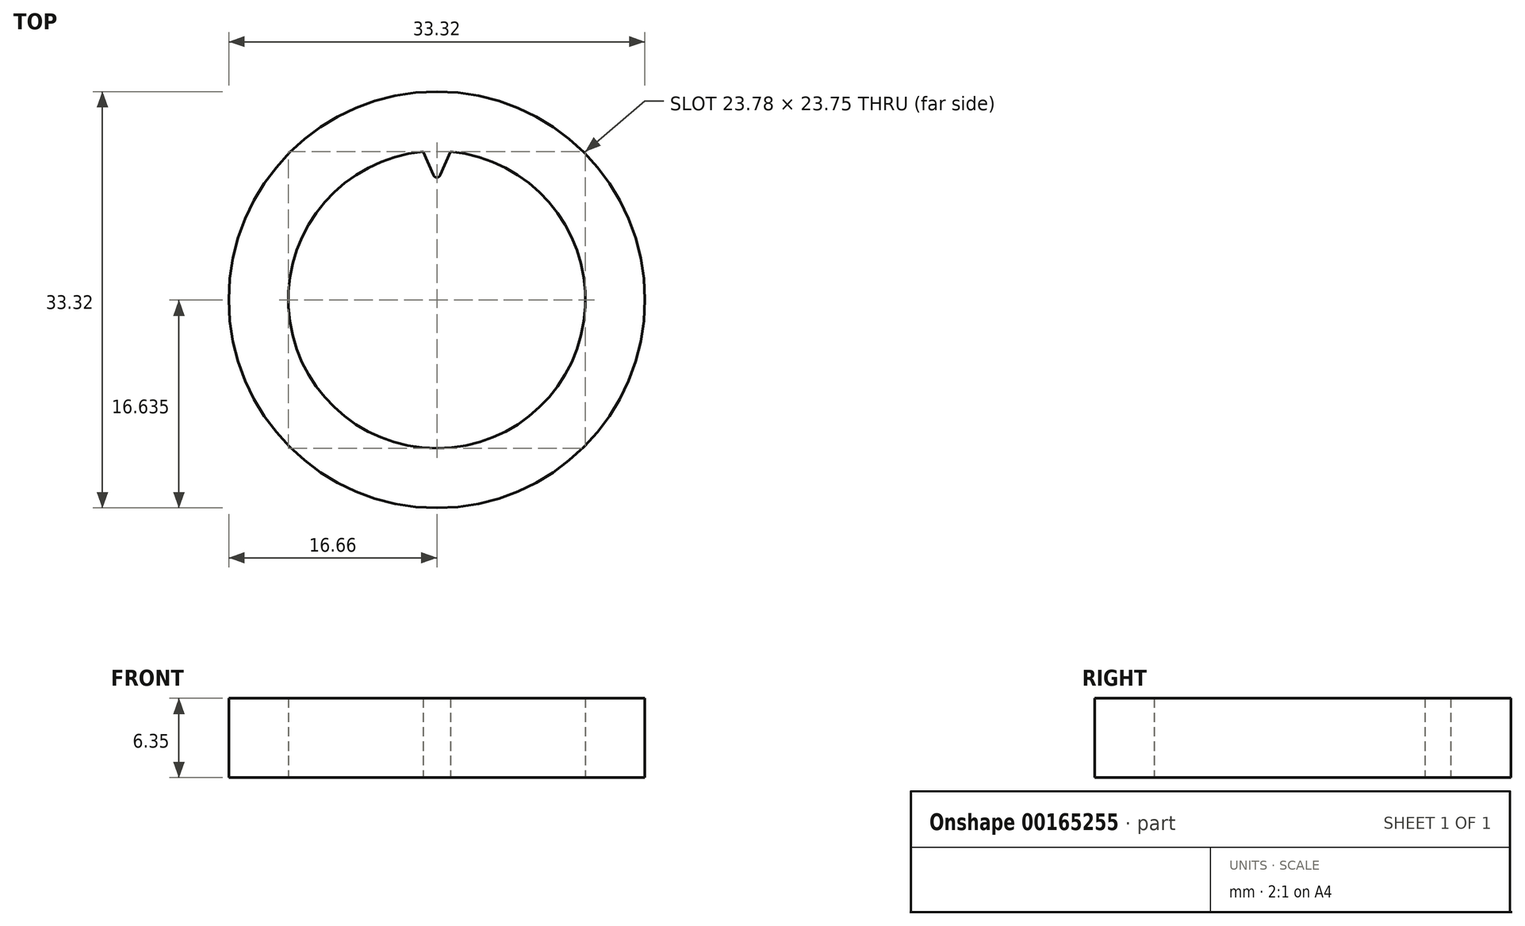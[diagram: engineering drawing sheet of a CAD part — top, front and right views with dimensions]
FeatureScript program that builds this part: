
annotation { "Feature Type Name" : "Feature", "Feature Type Description" : "" }
export const myFeature = defineFeature(function(context is Context, id is Id, definition is map)
    precondition{}
    {
        {
            var Q0;
            Q0=qCreatedBy(makeId("Top.planeOp"),FACE);
            var sketch = newSketch(context, id + "F0", { "sketchPlane" : qUnion([Q0])});
            skCircle(sketch, "E0", {"center": v(0, 0) * mm, "radius": 11.9 * mm});
            skSolve(sketch);
        }
        {
            var Q0;
            Q0 = qSketchRegion(id + "F0", true);
            extrude(context, id + "F1", {"entities" : qUnion([Q0]), "depth" : 6.35 * mm});
        }
        {
            var Q0;
            Q0=makeQuery(id+"F1.opExtrude","CAP_FACE",FACE,{"disambiguationData":[OSD([sQuery(id+"F0.wireOp",EDGE,"E0")])],"isStart":false});
            var sketch = newSketch(context, id + "F2", { "sketchPlane" : qUnion([Q0])});
            skLineSegment(sketch, "E1", {"start": v(0, 0) * mm, "end": v(0, 11.9) * mm, "construction": true});
            skLineSegment(sketch, "E2", {"start": v(0, 0) * mm, "end": v(0.74, 11.88) * mm, "construction": true});
            skArc(sketch, "E3", {"start": v(1.1, 11.85) * mm, "mid": v(0, 11.9) * mm, "end": v(-1.1, 11.85) * mm});
            skArc(sketch, "E4", {"start": v(-0.27, 9.97) * mm, "mid": v(0, 9.79) * mm, "end": v(0.27, 9.97) * mm});
            skLineSegment(sketch, "E5", {"start": v(-0.27, 9.97) * mm, "end": v(-1.1, 11.85) * mm});
            skLineSegment(sketch, "E6", {"start": v(0.27, 9.97) * mm, "end": v(1.1, 11.85) * mm});
            skPoint(sketch, "E7", {"position": v(0.68, 10.9) * mm});
            skSolve(sketch);
        }
        {
            var Q0;
            Q0 = qSketchRegion(id + "F2", true);
            var Q1;
            Q1=makeQuery(id+"F1.opExtrude","CAP_FACE",FACE,{"disambiguationData":[OSD([sQuery(id+"F0.wireOp",EDGE,"E0")])],"isStart":true});
            extrude(context, id + "F3", {"entities" : qUnion([Q0]), "operationType" : NewBodyOperationType.REMOVE, "endBound" : BoundingType.UP_TO_SURFACE, "oppositeDirection" : true, "endBoundEntityFace" : qUnion([Q1]), "depth" : 25.4 * mm});
        }
        {
            var Q0;
            Q0=makeQuery(id+"F1.opExtrude","CAP_FACE",FACE,{"disambiguationData":[OSD([sQuery(id+"F0.wireOp",EDGE,"E0")])],"isStart":false});
            var sketch = newSketch(context, id + "F4", { "sketchPlane" : qUnion([Q0])});
            skCircle(sketch, "E8", {"center": v(0, 0) * mm, "radius": 16.66 * mm});
            skSolve(sketch);
        }
        {
            var Q0;
            Q0=makeQuery(id+"F4.imprint","IMPRINT",FACE,{"disambiguationData":[TD([[makeQuery(id+"F4.imprint","IMPRINT",EDGE,{"derivedFrom":sQuery(id+"F4.wireOp",EDGE,"E8")}),1.0]])]});
            extrude(context, id + "F5", {"entities" : qUnion([Q0]), "depth" : 6.35 * mm});
        }
        {
            var Q0;
            Q0=makeQuery(id+"F1.opExtrude","CAP_FACE",FACE,{"disambiguationData":[OSD([sQuery(id+"F0.wireOp",EDGE,"E0")])],"isStart":true});
            var Q1;
            Q1=makeQuery(id+"F5.opExtrude","CAP_FACE",FACE,{"disambiguationData":[OSD([sQuery(id+"F0.wireOp",EDGE,"E0"),sQuery(id+"F2.wireOp",EDGE,"E4"),sQuery(id+"F2.wireOp",EDGE,"E5"),sQuery(id+"F2.wireOp",EDGE,"E6"),sQuery(id+"F4.wireOp",EDGE,"E8")])],"isStart":true});
            extrude(context, id + "F6", {"entities" : qUnion([Q0]), "operationType" : NewBodyOperationType.REMOVE, "endBound" : BoundingType.UP_TO_SURFACE, "oppositeDirection" : true, "endBoundEntityFace" : qUnion([Q1]), "depth" : 25.4 * mm});
        }
    });
